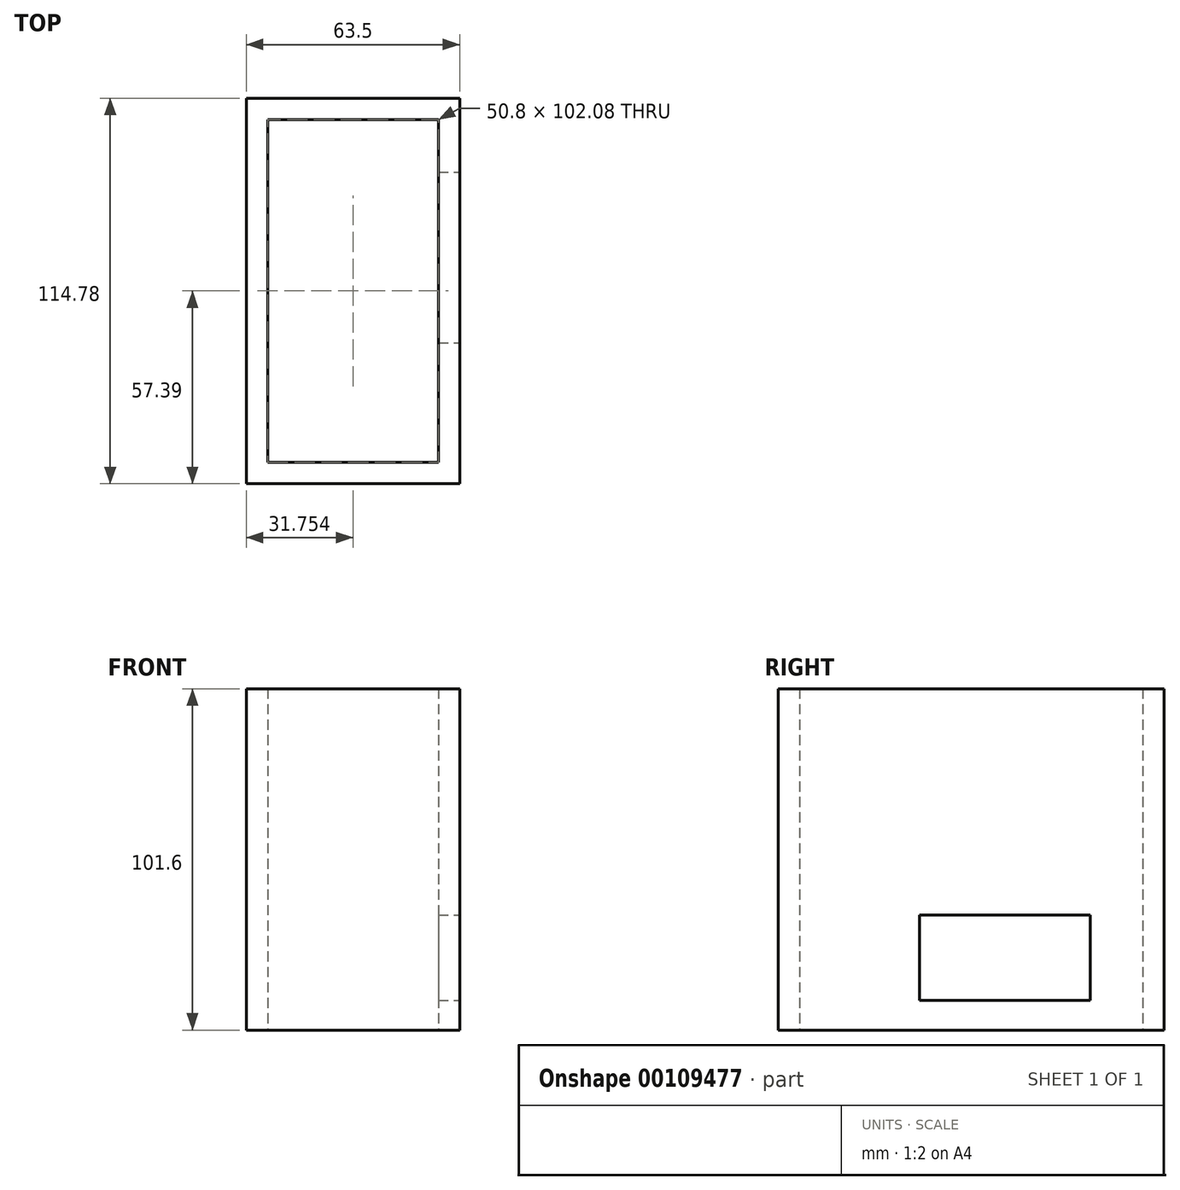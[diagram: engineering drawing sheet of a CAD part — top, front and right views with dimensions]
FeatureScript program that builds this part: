
annotation { "Feature Type Name" : "Feature", "Feature Type Description" : "" }
export const myFeature = defineFeature(function(context is Context, id is Id, definition is map)
    precondition{}
    {
        {
            var Q0;
            Q0=qCreatedBy(makeId("Top.planeOp"),FACE);
            var sketch = newSketch(context, id + "F0", { "sketchPlane" : qUnion([Q0])});
            skLineSegment(sketch, "E0.bottom", {"start": v(-29.69, 74.96) * mm, "end": v(33.81, 74.96) * mm});
            skLineSegment(sketch, "E0.top", {"start": v(-29.69, -39.82) * mm, "end": v(33.81, -39.82) * mm});
            skLineSegment(sketch, "E0.left", {"start": v(-29.69, 74.96) * mm, "end": v(-29.69, -39.82) * mm});
            skLineSegment(sketch, "E0.right", {"start": v(33.81, 74.96) * mm, "end": v(33.81, -39.82) * mm});
            skLineSegment(sketch, "E1", {"start": v(-29.69, 68.61) * mm, "end": v(-23.34, 68.61) * mm, "construction": true});
            skLineSegment(sketch, "E2.bottom", {"start": v(-23.34, 68.61) * mm, "end": v(27.46, 68.61) * mm});
            skLineSegment(sketch, "E2.top", {"start": v(-23.34, -33.47) * mm, "end": v(27.46, -33.47) * mm});
            skLineSegment(sketch, "E2.left", {"start": v(-23.34, 68.61) * mm, "end": v(-23.34, -33.47) * mm});
            skLineSegment(sketch, "E2.right", {"start": v(27.46, 68.61) * mm, "end": v(27.46, -33.47) * mm});
            skSolve(sketch);
        }
        {
            var Q0;
            Q0=makeQuery(id+"F0.imprint","IMPRINT",FACE,{"disambiguationData":[TD([[makeQuery(id+"F0.imprint","IMPRINT",EDGE,{"derivedFrom":sQuery(id+"F0.wireOp",EDGE,"E0.bottom")}),-1.0]])]});
            extrude(context, id + "F1", {"entities" : qUnion([Q0]), "depth" : 101.6 * mm});
        }
        {
            var Q0;
            Q0=makeQuery(id+"F1.opExtrude","SWEPT_FACE",FACE,{"disambiguationData":[OSD([sQuery(id+"F0.wireOp",EDGE,"E0.right")])]});
            var sketch = newSketch(context, id + "F2", { "sketchPlane" : qUnion([Q0])});
            skLineSegment(sketch, "E3.0", {"start": v(-39.82, 101.6) * mm, "end": v(-39.82, 0) * mm});
            skLineSegment(sketch, "E4.0", {"start": v(74.96, 101.6) * mm, "end": v(74.96, 0) * mm});
            skLineSegment(sketch, "E5.0", {"start": v(74.96, 101.6) * mm, "end": v(-39.82, 101.6) * mm});
            skLineSegment(sketch, "E6.0", {"start": v(74.96, 0) * mm, "end": v(-39.82, 0) * mm});
            skLineSegment(sketch, "E7.bottom", {"start": v(52.92, 34.29) * mm, "end": v(2.12, 34.29) * mm});
            skLineSegment(sketch, "E7.top", {"start": v(52.92, 8.9) * mm, "end": v(2.12, 8.9) * mm});
            skLineSegment(sketch, "E7.left", {"start": v(52.92, 34.29) * mm, "end": v(52.92, 8.9) * mm});
            skLineSegment(sketch, "E7.right", {"start": v(2.12, 34.29) * mm, "end": v(2.12, 8.9) * mm});
            skSolve(sketch);
        }
        {
            var Q0;
            Q0=makeQuery(id+"F2.imprint","IMPRINT",FACE,{"disambiguationData":[TD([[makeQuery(id+"F2.imprint","IMPRINT",EDGE,{"derivedFrom":sQuery(id+"F2.wireOp",EDGE,"E7.bottom")}),1.0]])]});
            extrude(context, id + "F3", {"entities" : qUnion([Q0]), "operationType" : NewBodyOperationType.REMOVE, "oppositeDirection" : true, "depth" : 25.4 * mm});
        }
    });
